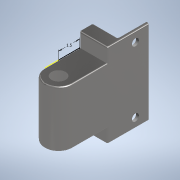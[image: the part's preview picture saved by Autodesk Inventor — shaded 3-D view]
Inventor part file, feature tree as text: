
AUTODESK INVENTOR PART (.ipt)
format: ipt  version: 2022 (Build 260153000, 153)  size: 174,080 bytes
history: native  units: mm (DEFAULTED — no unit token found)
features: sketch x4, extrude x4, fillet x2
ambient origin geometry x8: Origin, YZ Plane, XZ Plane, XY Plane, X Axis, Y Axis, Z Axis, Center Point
bodies: Solid1 (feature_tree)
feature tree (10):
  sketch  "Sketch1"  dims[d3=40.0mm d4=0.0mm d5=50.0mm d6=10.0mm d7=0.0mm d8=0.0mm]
  extrude  "Extrusion1"  Depth=10.0mm TaperAngle=0.0deg
  extrude  "Extrusion2"  Depth=2.0mm
  sketch  "Sketch2"  dims[d9=15.0mm d11=2.0mm]
  extrude  "Extrusion3"  Depth=1.0mm
  fillet  "Fillet1"  Radius=1.0mm
  fillet  "Fillet2"  Radius=10.0mm
  extrude  "Extrusion4"  Depth=10.0mm
  sketch  "Sketch3"  dims[d12=20.0mm d13=0.0mm d14=1.0mm d15=1.0mm d16=10.0mm]
  sketch  "Sketch4"  dims[d17=20.0mm d18=25.0mm d19=10.0mm d20=5.0mm d21=5.0mm d22=0.0mm d23=0.0mm d24=46.568542mm d25=6.715mm d10=5.0mm]
